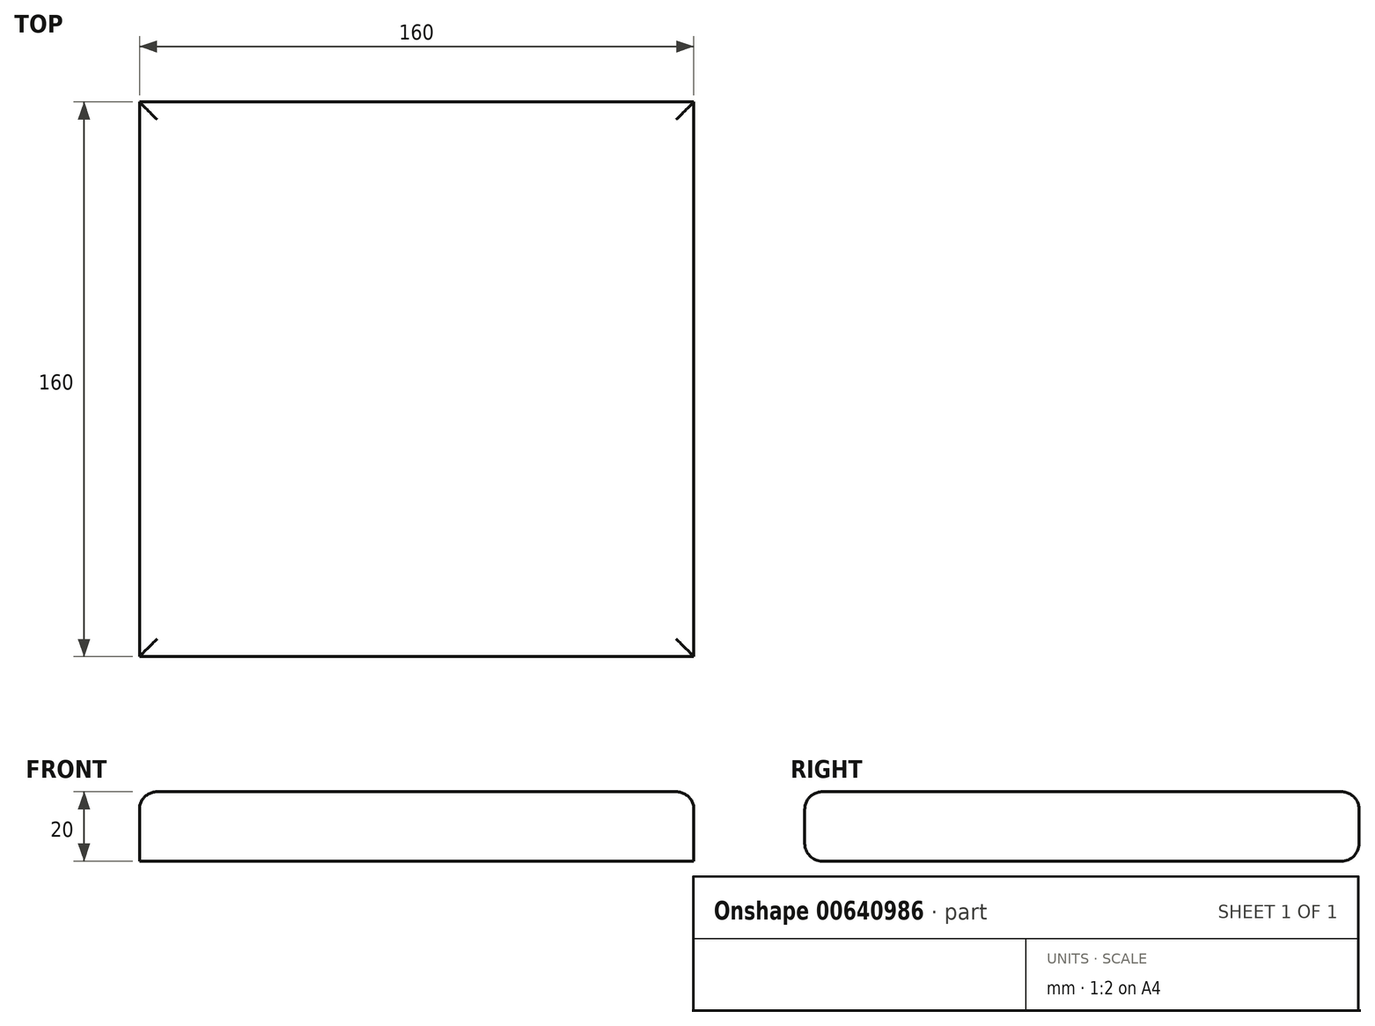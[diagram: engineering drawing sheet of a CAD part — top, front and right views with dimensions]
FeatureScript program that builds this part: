
annotation { "Feature Type Name" : "Feature", "Feature Type Description" : "" }
export const myFeature = defineFeature(function(context is Context, id is Id, definition is map)
    precondition{}
    {
        {
            var Q0;
            Q0=qCreatedBy(makeId("Top.planeOp"),FACE);
            var sketch = newSketch(context, id + "F0", { "sketchPlane" : qUnion([Q0])});
            skLineSegment(sketch, "E0.bottom", {"start": v(-81.12, 77.82) * mm, "end": v(78.88, 77.82) * mm});
            skLineSegment(sketch, "E0.top", {"start": v(-81.12, -82.18) * mm, "end": v(78.88, -82.18) * mm});
            skLineSegment(sketch, "E0.left", {"start": v(-81.12, 77.82) * mm, "end": v(-81.12, -82.18) * mm});
            skLineSegment(sketch, "E0.right", {"start": v(78.88, 77.82) * mm, "end": v(78.88, -82.18) * mm});
            skSolve(sketch);
        }
        {
            var Q0;
            Q0=makeQuery(id+"F0.imprint","IMPRINT",FACE,{"disambiguationData":[TD([[makeQuery(id+"F0.imprint","IMPRINT",EDGE,{"derivedFrom":sQuery(id+"F0.wireOp",EDGE,"E0.bottom")}),-1.0]])]});
            extrude(context, id + "F1", {"entities" : qUnion([Q0]), "depth" : 20 * mm, "offsetDistance" : 25.4 * mm});
        }
        {
            var Q0;
            Q0=makeQuery(id+"F1.opExtrude","CAP_EDGE",EDGE,{"disambiguationData":[OSD([sQuery(id+"F0.wireOp",EDGE,"E0.bottom")])],"isStart":false});
            var Q1;
            Q1=makeQuery(id+"F1.opExtrude","CAP_FACE",FACE,{"disambiguationData":[OSD([sQuery(id+"F0.wireOp",EDGE,"E0.bottom"),sQuery(id+"F0.wireOp",EDGE,"E0.top"),sQuery(id+"F0.wireOp",EDGE,"E0.left"),sQuery(id+"F0.wireOp",EDGE,"E0.right")])],"isStart":false});
            fillet(context, id + "F2", {"entities" : qUnion([Q0, Q1]), "radius" : 5.08 * mm, "tangentPropagation" : true, "allowEdgeOverflow" : false});
        }
        {
            var Q0;
            Q0=makeQuery(id+"F1.opExtrude","CAP_EDGE",EDGE,{"disambiguationData":[OSD([sQuery(id+"F0.wireOp",EDGE,"E0.top")])],"isStart":true});
            fillet(context, id + "F3", {"entities" : qUnion([Q0]), "radius" : 5.08 * mm, "tangentPropagation" : true, "allowEdgeOverflow" : false});
        }
        {
            var Q0;
            Q0=makeQuery(id+"F1.opExtrude","CAP_EDGE",EDGE,{"disambiguationData":[OSD([sQuery(id+"F0.wireOp",EDGE,"E0.bottom")])],"isStart":true});
            fillet(context, id + "F4", {"entities" : qUnion([Q0]), "radius" : 5.08 * mm, "tangentPropagation" : true, "allowEdgeOverflow" : false});
        }
    });
